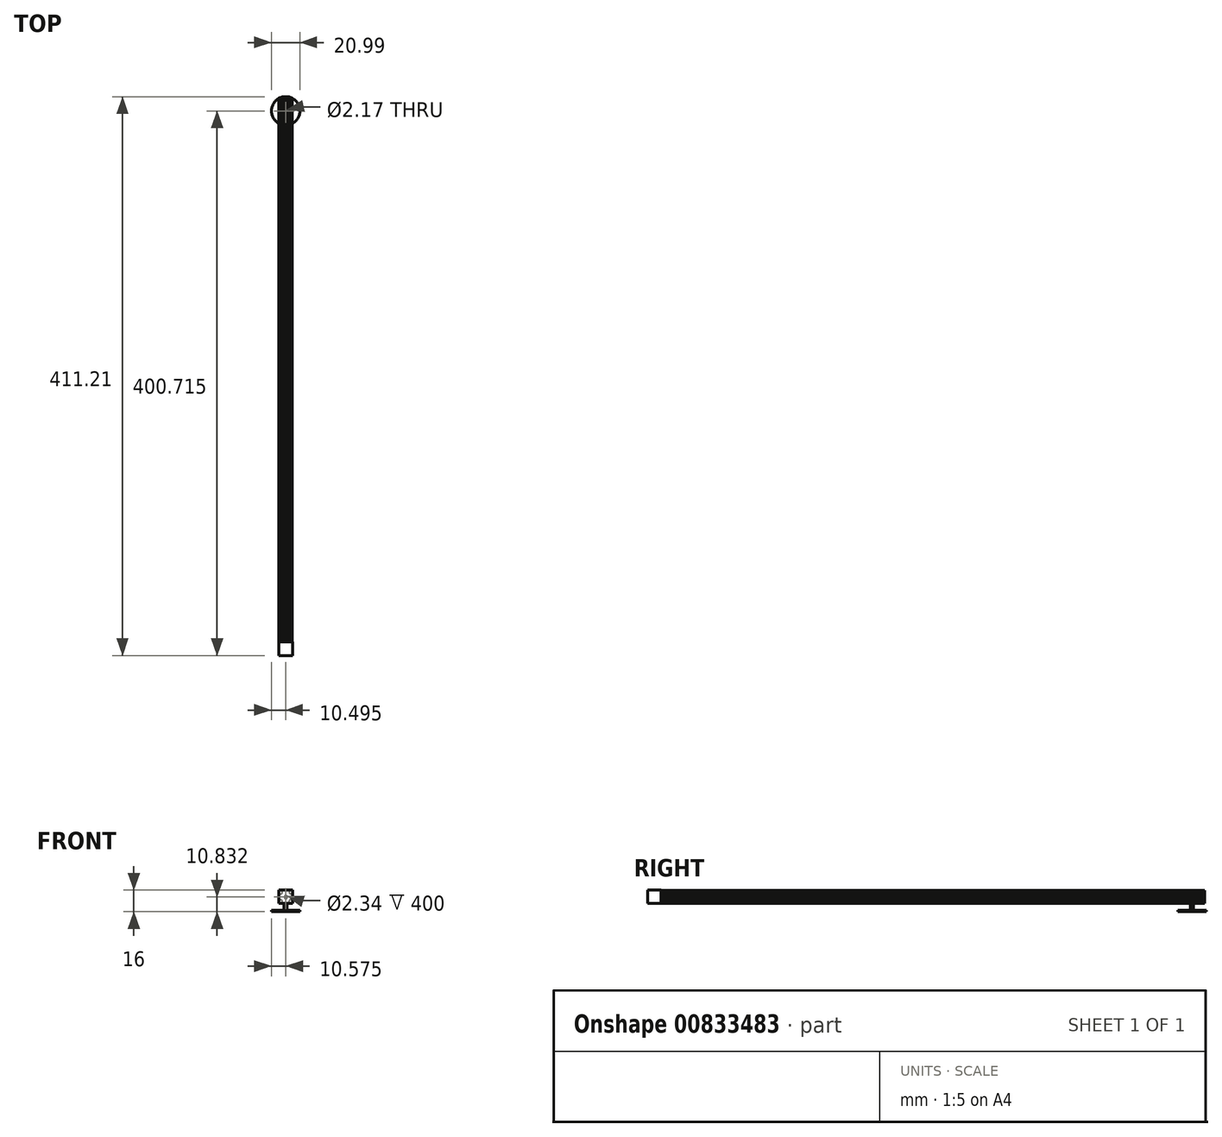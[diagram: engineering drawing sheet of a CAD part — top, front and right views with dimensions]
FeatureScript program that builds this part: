
annotation { "Feature Type Name" : "Feature", "Feature Type Description" : "" }
export const myFeature = defineFeature(function(context is Context, id is Id, definition is map)
    precondition{}
    {
        {
            var Q0;
            Q0=qCreatedBy(makeId("Front.planeOp"),FACE);
            var sketch = newSketch(context, id + "F0", { "sketchPlane" : qUnion([Q0])});
            skLineSegment(sketch, "E0.bottom", {"start": v(-10, 10) * mm, "end": v(0, 10) * mm});
            skLineSegment(sketch, "E0.top", {"start": v(-10, 0) * mm, "end": v(0, 0) * mm});
            skLineSegment(sketch, "E0.left", {"start": v(-10, 10) * mm, "end": v(-10, 0) * mm});
            skLineSegment(sketch, "E0.right", {"start": v(0, 10) * mm, "end": v(0, 0) * mm});
            skSolve(sketch);
        }
        {
            var Q0;
            Q0=makeQuery(id+"F0.imprint","IMPRINT",FACE,{"disambiguationData":[TD([[makeQuery(id+"F0.imprint","IMPRINT",EDGE,{"derivedFrom":sQuery(id+"F0.wireOp",EDGE,"E0.bottom")}),-1.0]])]});
            extrude(context, id + "F1", {"entities" : qUnion([Q0]), "depth" : 10 * mm, "offsetDistance" : 25.4 * mm});
        }
        {
            var Q0;
            Q0=makeQuery(id+"F1.opExtrude","CAP_FACE",FACE,{"disambiguationData":[OSD([sQuery(id+"F0.wireOp",EDGE,"E0.bottom"),sQuery(id+"F0.wireOp",EDGE,"E0.top"),sQuery(id+"F0.wireOp",EDGE,"E0.left"),sQuery(id+"F0.wireOp",EDGE,"E0.right")])],"isStart":true});
            var sketch = newSketch(context, id + "F2", { "sketchPlane" : qUnion([Q0])});
            skCircle(sketch, "E1.cCircle", {"center": v(5, 4.86) * mm, "radius": 4.86 * mm, "construction": true});
            skPoint(sketch, "E1.cCircle.centerSnap0", {"position": v(5, 0) * mm});
            skLineSegment(sketch, "E1.0", {"start": v(6.03, 0) * mm, "end": v(3.97, 0) * mm});
            skLineSegment(sketch, "E1.1", {"start": v(3.97, 0) * mm, "end": v(2.08, 0.84) * mm});
            skLineSegment(sketch, "E1.2", {"start": v(2.08, 0.84) * mm, "end": v(0.7, 2.37) * mm});
            skLineSegment(sketch, "E1.3", {"start": v(0.7, 2.37) * mm, "end": v(0.06, 4.34) * mm});
            skLineSegment(sketch, "E1.4", {"start": v(0.06, 4.34) * mm, "end": v(0.28, 6.4) * mm});
            skLineSegment(sketch, "E1.5", {"start": v(0.28, 6.4) * mm, "end": v(1.3, 8.18) * mm});
            skLineSegment(sketch, "E1.6", {"start": v(1.3, 8.18) * mm, "end": v(2.98, 9.4) * mm});
            skLineSegment(sketch, "E1.7", {"start": v(2.98, 9.4) * mm, "end": v(5, 9.82) * mm});
            skLineSegment(sketch, "E1.8", {"start": v(5, 9.82) * mm, "end": v(7.02, 9.4) * mm});
            skLineSegment(sketch, "E1.9", {"start": v(7.02, 9.4) * mm, "end": v(8.7, 8.18) * mm});
            skLineSegment(sketch, "E1.10", {"start": v(8.7, 8.18) * mm, "end": v(9.72, 6.4) * mm});
            skLineSegment(sketch, "E1.11", {"start": v(9.72, 6.4) * mm, "end": v(9.94, 4.34) * mm});
            skLineSegment(sketch, "E1.12", {"start": v(9.94, 4.34) * mm, "end": v(9.3, 2.37) * mm});
            skLineSegment(sketch, "E1.13", {"start": v(9.3, 2.37) * mm, "end": v(7.92, 0.84) * mm});
            skLineSegment(sketch, "E1.14", {"start": v(7.92, 0.84) * mm, "end": v(6.03, 0) * mm});
            skPoint(sketch, "E1.0.midPoint", {"position": v(5, 0) * mm});
            skSolve(sketch);
        }
        {
            var Q0;
            Q0=makeQuery(id+"F2.imprint","IMPRINT",FACE,{"disambiguationData":[TD([[makeQuery(id+"F2.imprint","IMPRINT",EDGE,{"derivedFrom":sQuery(id+"F2.wireOp",EDGE,"E1.0")}),-1.0]])]});
            var sketch = newSketch(context, id + "F3", { "sketchPlane" : qUnion([Q0])});
            skCircle(sketch, "E2", {"center": v(8.58, 8.17) * mm, "radius": 1.1 * mm});
            skCircle(sketch, "E3", {"center": v(8.51, 1.55) * mm, "radius": 1.05 * mm});
            skCircle(sketch, "E4", {"center": v(4.92, 4.83) * mm, "radius": 1.17 * mm});
            skCircle(sketch, "E5", {"center": v(1.4, 1.52) * mm, "radius": 1.22 * mm});
            skCircle(sketch, "E6", {"center": v(1.35, 8.38) * mm, "radius": 1.1 * mm});
            skSolve(sketch);
        }
        {
            var Q0;
            Q0=makeQuery(id+"F3.imprint","IMPRINT",FACE,{"disambiguationData":[TD([[makeQuery(id+"F3.imprint","IMPRINT",EDGE,{"derivedFrom":sQuery(id+"F3.wireOp",EDGE,"E4")}),-1.0]])]});
            extrude(context, id + "F4", {"entities" : qUnion([Q0]), "operationType" : NewBodyOperationType.ADD, "depth" : 400 * mm, "offsetDistance" : 25.4 * mm});
        }
        {
            var Q0;
            Q0=makeQuery(id+"F4.boolean.opBoolean","MERGE",FACE,{"derivedFrom":[makeQuery(id+"F1.opExtrude","SWEPT_FACE",FACE,{"disambiguationData":[OSD([sQuery(id+"F0.wireOp",EDGE,"E0.top")])]}),makeQuery(id+"F4.opExtrude","SWEPT_FACE",FACE,{"disambiguationData":[OSD([sQuery(id+"F2.wireOp",EDGE,"E1.0")])]})]});
            var sketch = newSketch(context, id + "F5", { "sketchPlane" : qUnion([Q0])});
            skLineSegment(sketch, "E7.bottom", {"start": v(-11.65, -387) * mm, "end": v(2.03, -387) * mm});
            skLineSegment(sketch, "E7.top", {"start": v(-11.65, -394.9) * mm, "end": v(2.03, -394.9) * mm});
            skLineSegment(sketch, "E7.left", {"start": v(-11.65, -387) * mm, "end": v(-11.65, -394.9) * mm});
            skLineSegment(sketch, "E7.right", {"start": v(2.03, -387) * mm, "end": v(2.03, -394.9) * mm});
            skSolve(sketch);
        }
        {
            var Q0;
            {var subQ0=sQuery(id+"F5.wireOp",EDGE,"E7.bottom");var subQ1=sQuery(id+"F2.wireOp",EDGE,"E1.0");var subQ2=makeQuery(id+"F4.opExtrude","SWEPT_EDGE",EDGE,{"disambiguationData":[OSD([subQ1,sQuery(id+"F2.wireOp",EDGE,"E1.14")])]});var subQ3=makeQuery(id+"F5.imprint","INTERSECT",VERTEX,{"derivedFrom":[subQ2,subQ0]});Q0=makeQuery(id+"F5.imprint","IMPRINT",FACE,{"disambiguationData":[TD([[makeQuery(id+"F5.imprint","IMPRINT",EDGE,{"disambiguationData":[TD([[subQ3,-1.0]])],"derivedFrom":subQ0}),-1.0]])]});}
            var sketch = newSketch(context, id + "F6", { "sketchPlane" : qUnion([Q0])});
            skCircle(sketch, "E8", {"center": v(-5, -390.72) * mm, "radius": 1.09 * mm});
            skSolve(sketch);
        }
        {
            var Q0;
            Q0 = qSketchRegion(id + "F6", true);
            extrude(context, id + "F7", {"entities" : qUnion([Q0]), "depth" : 5 * mm, "offsetDistance" : 25.4 * mm});
        }
        {
            var Q0;
            Q0=makeQuery(id+"F7.opExtrude","CAP_FACE",FACE,{"disambiguationData":[OSD([sQuery(id+"F6.wireOp",EDGE,"E8")])],"isStart":false});
            var sketch = newSketch(context, id + "F8", { "sketchPlane" : qUnion([Q0])});
            skCircle(sketch, "E9", {"center": v(-5, -390.72) * mm, "radius": 10.5 * mm});
            skSolve(sketch);
        }
        {
            var Q0;
            Q0=makeQuery(id+"F8.imprint","IMPRINT",FACE,{"disambiguationData":[TD([[makeQuery(id+"F8.imprint","IMPRINT",EDGE,{"derivedFrom":sQuery(id+"F8.wireOp",EDGE,"E9")}),1.0]])]});
            extrude(context, id + "F9", {"entities" : qUnion([Q0]), "depth" : 1 * mm, "offsetDistance" : 25.4 * mm});
        }
    });
